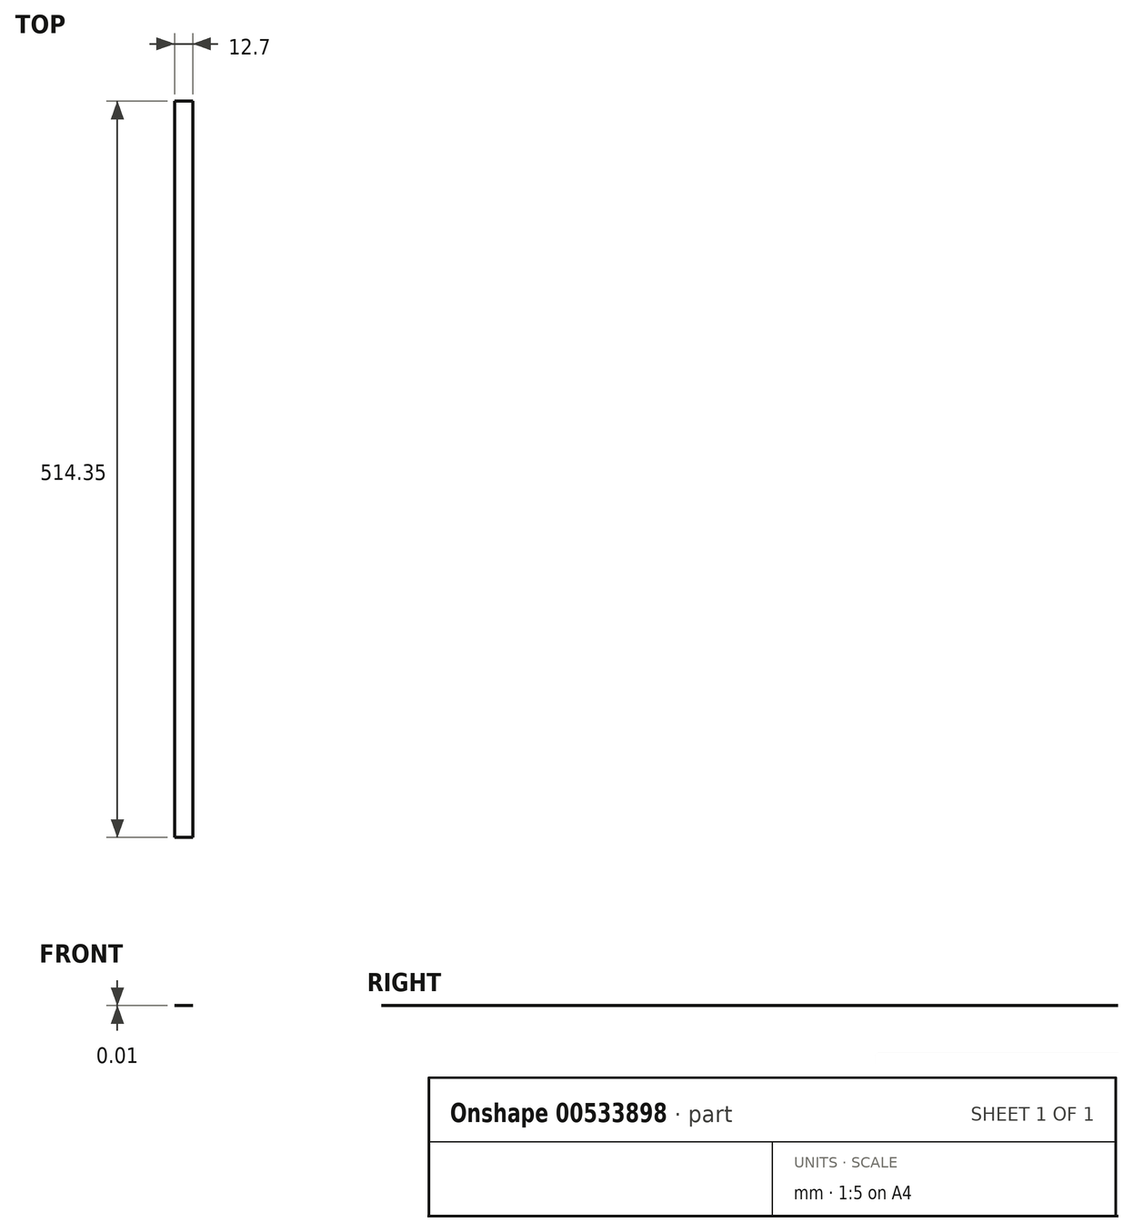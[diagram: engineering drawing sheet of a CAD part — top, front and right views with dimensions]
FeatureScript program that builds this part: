
annotation { "Feature Type Name" : "Feature", "Feature Type Description" : "" }
export const myFeature = defineFeature(function(context is Context, id is Id, definition is map)
    precondition{}
    {
        {
            var Q0;
            Q0=qCreatedBy(makeId("Top.planeOp"),FACE);
            var sketch = newSketch(context, id + "F0", { "sketchPlane" : qUnion([Q0])});
            skLineSegment(sketch, "E0", {"start": v(-12.7, 224.18) * mm, "end": v(-12.7, -290.17) * mm});
            skLineSegment(sketch, "E1", {"start": v(-12.7, -290.17) * mm, "end": v(0, -290.17) * mm});
            skLineSegment(sketch, "E2", {"start": v(0, -290.17) * mm, "end": v(0, 224.18) * mm});
            skLineSegment(sketch, "E3", {"start": v(-12.7, 224.18) * mm, "end": v(0, 224.18) * mm});
            skSolve(sketch);
        }
        {
            var Q0;
            Q0 = qSketchRegion(id + "F0", true);
            extrude(context, id + "F1", {"entities" : qUnion([Q0]), "depth" : 0 * mm, "offsetDistance" : 25.4 * mm});
        }
    });
